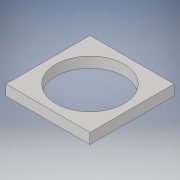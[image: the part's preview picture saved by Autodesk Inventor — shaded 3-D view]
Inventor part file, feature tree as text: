
AUTODESK INVENTOR PART (.ipt)
format: ipt  version: 2018 (Build 220112000, 112)  size: 102,912 bytes
history: native  units: in
note: dims shown in document units (in); Inventor stores cm internally (conversion verified against a paired STEP export)
features: extrude x1, sketch x1
ambient origin geometry x8: Origin, YZ Plane, XZ Plane, XY Plane, X Axis, Y Axis, Z Axis, Center Point
bodies: Body1 (feature_tree)
feature tree (2):
  extrude  "Extrusion2"  Depth=0.8in
  sketch  "Sketch1"  dims[d0=0.65in d4=0.8in d5=0.4in d6=0.8in d7=0.4in d8=0.1in d9=0.0in]
